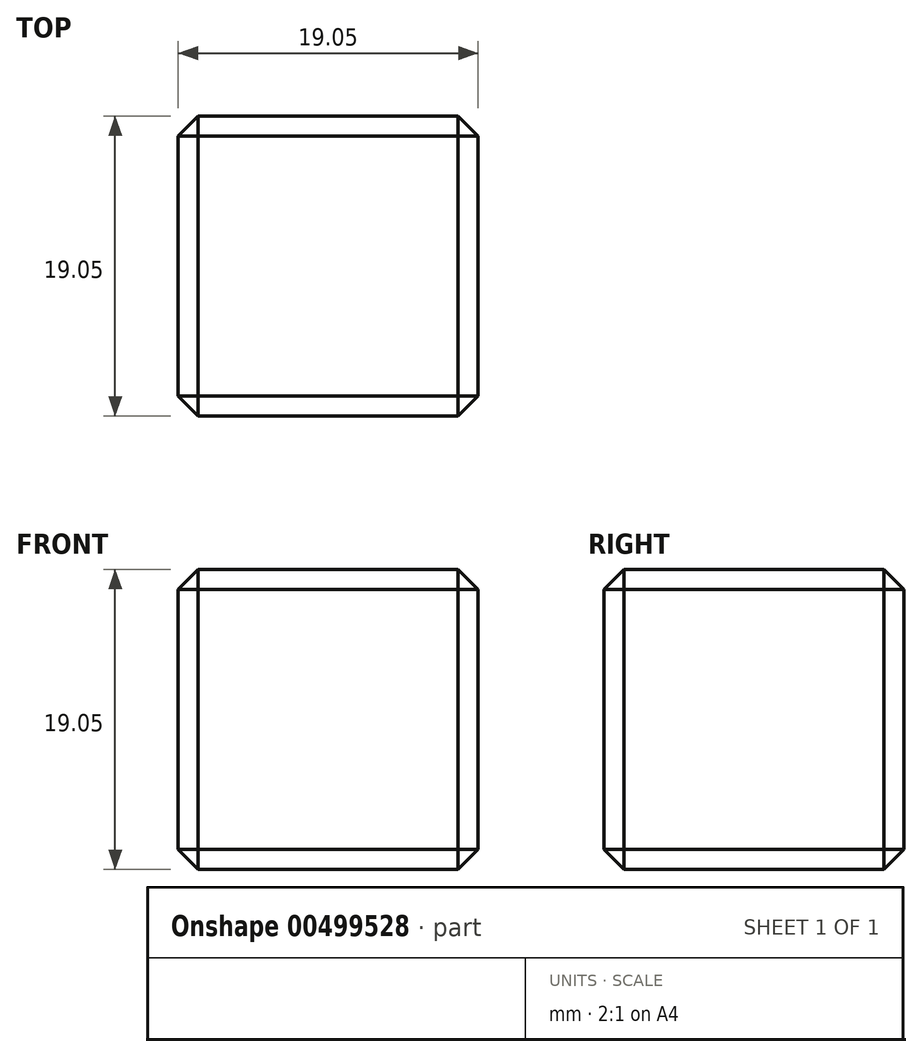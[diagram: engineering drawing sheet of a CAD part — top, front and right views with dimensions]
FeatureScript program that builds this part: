
annotation { "Feature Type Name" : "Feature", "Feature Type Description" : "" }
export const myFeature = defineFeature(function(context is Context, id is Id, definition is map)
    precondition{}
    {
        {
            var Q0;
            Q0=qCreatedBy(makeId("Top.planeOp"),FACE);
            var sketch = newSketch(context, id + "F0", { "sketchPlane" : qUnion([Q0])});
            skLineSegment(sketch, "E0.bottom", {"start": v(-11.43, 15.78) * mm, "end": v(7.62, 15.78) * mm});
            skLineSegment(sketch, "E0.top", {"start": v(-11.43, -3.27) * mm, "end": v(7.62, -3.27) * mm});
            skLineSegment(sketch, "E0.left", {"start": v(-11.43, 15.78) * mm, "end": v(-11.43, -3.27) * mm});
            skLineSegment(sketch, "E0.right", {"start": v(7.62, 15.78) * mm, "end": v(7.62, -3.27) * mm});
            skSolve(sketch);
        }
        {
            var Q0;
            Q0 = qSketchRegion(id + "F0", true);
            extrude(context, id + "F1", {"entities" : qUnion([Q0]), "depth" : 19.05 * mm});
        }
        {
            var Q0;
            Q0=makeQuery(id+"F1.opExtrude","CAP_FACE",FACE,{"disambiguationData":[OSD([sQuery(id+"F0.wireOp",EDGE,"E0.bottom"),sQuery(id+"F0.wireOp",EDGE,"E0.top"),sQuery(id+"F0.wireOp",EDGE,"E0.left"),sQuery(id+"F0.wireOp",EDGE,"E0.right")])],"isStart":false});
            var Q1;
            Q1=makeQuery(id+"F1.opExtrude","CAP_FACE",FACE,{"disambiguationData":[OSD([sQuery(id+"F0.wireOp",EDGE,"E0.bottom"),sQuery(id+"F0.wireOp",EDGE,"E0.top"),sQuery(id+"F0.wireOp",EDGE,"E0.left"),sQuery(id+"F0.wireOp",EDGE,"E0.right")])],"isStart":true});
            var Q2;
            Q2=makeQuery(id+"F1.opExtrude","SWEPT_EDGE",EDGE,{"disambiguationData":[OSD([sQuery(id+"F0.wireOp",EDGE,"E0.top"),sQuery(id+"F0.wireOp",EDGE,"E0.right")])]});
            var Q3;
            Q3=makeQuery(id+"F1.opExtrude","SWEPT_EDGE",EDGE,{"disambiguationData":[OSD([sQuery(id+"F0.wireOp",EDGE,"E0.bottom"),sQuery(id+"F0.wireOp",EDGE,"E0.right")])]});
            var Q4;
            Q4=makeQuery(id+"F1.opExtrude","SWEPT_EDGE",EDGE,{"disambiguationData":[OSD([sQuery(id+"F0.wireOp",EDGE,"E0.bottom"),sQuery(id+"F0.wireOp",EDGE,"E0.left")])]});
            var Q5;
            Q5=makeQuery(id+"F1.opExtrude","SWEPT_EDGE",EDGE,{"disambiguationData":[OSD([sQuery(id+"F0.wireOp",EDGE,"E0.top"),sQuery(id+"F0.wireOp",EDGE,"E0.left")])]});
            chamfer(context, id + "F2", {"entities" : qUnion([Q0, Q1, Q2, Q3, Q4, Q5]), "width" : 1.27 * mm, "tangentPropagation" : true});
        }
    });
